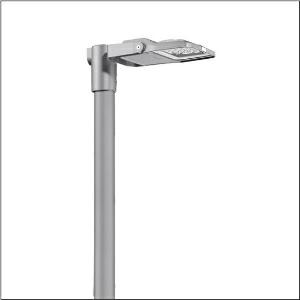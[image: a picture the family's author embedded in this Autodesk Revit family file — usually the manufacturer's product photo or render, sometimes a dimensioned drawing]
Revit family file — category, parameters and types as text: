
# Revit family: floodlight_fl_21_iq_micro___pl43_5xa7761a2a3a_2bb2
name_source: partatom
category: Lighting Fixtures
units: mm (PartAtom-declared; Revit-internal decimal feet)

## family parameters
Cut with Voids When Loaded = No
Host = Face
Light Source = No
Part Type = Normal
Room Calculation Point = No
Round Connector Dimension = Use Diameter
Shared = No

## types (1)
- --- (1 x LED, 3040 lm, 23.1 W, 3000K)
    Apparent Load = 23 VA
    CIE Flux Codes = 29 80 99 100 100
    Color Rendering = 70
    Color Temperature = 3000K
    Default Elevation = 1800 mm
    Description = Floodlight FL 21 iQ micro, floodlight, primary light control with lens, of PMMA, primary optical cover: protective disc, of toughened safety glass, transparent, light distribution: PL43, light emission: direct distribution, installation type: surface-mounted, LED, High Power LED, rated luminous flux: 3.040lm, luminous efficacy: 132lm/W, light colour: 730, colour temperature: 3000K, control: optimised constant luminous flux control (CLO 2.0), Desk-Remote (wireless, voltage-free reading and setting of iQ features in the workshop via application-optimized NFC function/RFID function), Light-Fading, Smart-Wire, Night-Set, Lumen-Switch, Temp-Guard, Auto-Match, with terminal, 6-pole, mains connection: 220..240V, AC, 50/60Hz, start of lifetime: 23W, end of service life: 24W, reduction: 11W, luminaire housing, of diecast aluminium, powder-coated, Siteco® metallic grey (DB 702S), corrosivity category C5 mid according to DIN EN ISO 12944, sealing non-destructively replaceable, please order mast flange separately, mast bracket, of steel, galvanised, powder-coated, Siteco® metallic grey (DB 702S), protection rating (complete): IP66, insulation class (complete): insulation class II (safety insulation), certification: CE, ENEC, VDE, protection symbol: D, impact resistance: IK07, permissible operating ambient temperature: -40..+40°C, permissible operating ambient temperature for outdoor applications: -40..+50°C, standard: DIN EN 12944, LABS conformity tested according to VDMA 24364:2018-05, packaging unit: 1 piece

Light Distribution: PL43
    Height = 65 mm
    Lamp = 1 x LED
    Lamp Light Flux = 3040 lm
    Lamp Power = 23.1 W
    Lamp count = 1
    Length = 312 mm
    Luminous efficacy = 132 lm/W
    Manufacturer = Siteco
    ModVariant = No
    Model = 5XA7761A2A3A
    Number of Poles = 1
    OnlyDefault = Yes
    Power Factor = 1
    Product Name = Floodlight FL 21 iQ micro | PL43
    Product group = floodlight | pylon top
    ProductGroupID = 6101
    Protection Class = Protection class II
    Protection Degree = IP 66
    RLX_Detail_Level = 1
    RLX_Emergency_Light_Flux = 0 lm
    RLX_Emergency_Type = 0
    RLX_Emergency_Type_DB = No
    RlxData = <blob elided: 101673 chars, md5=8a9646d5>
    Socket = socket
    Standby Power = 0 W
    System Light Flux = 3040 lm
    System Power = 23 W
    Type Comments = factory setting: luminous flux: 100 % | dim-lin: 254 | 455 mA
    Type Image = l_1007121.jpg
    URL = http://relux.com
    VarID = @adj_148091
    Voltage = 0 V
    Weight = 0.00 kg
    Width = 230 mm

## geometry (parser evidence)
native form markers: Blend x4, Sweep x12
no freeform markers — native parametric forms only
